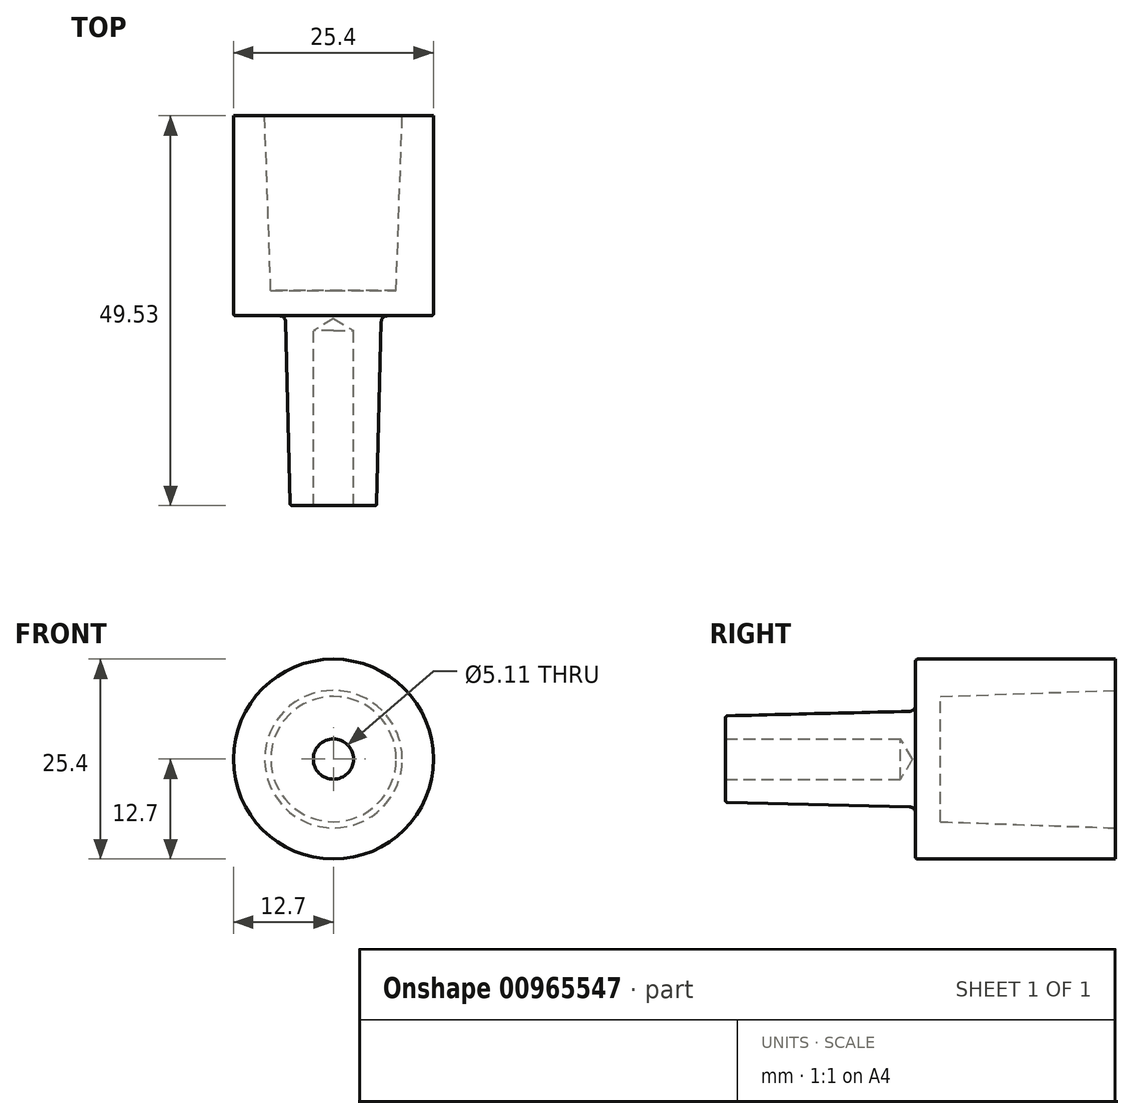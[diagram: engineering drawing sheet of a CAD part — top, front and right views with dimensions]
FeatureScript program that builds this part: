
annotation { "Feature Type Name" : "Feature", "Feature Type Description" : "" }
export const myFeature = defineFeature(function(context is Context, id is Id, definition is map)
    precondition{}
    {
        {
            var Q0;
            Q0=qCreatedBy(makeId("Right.planeOp"),FACE);
            var sketch = newSketch(context, id + "F0", { "sketchPlane" : qUnion([Q0])});
            skLineSegment(sketch, "E0", {"start": v(25.4, 0) * mm, "end": v(25.4, 12.7) * mm});
            skLineSegment(sketch, "E1", {"start": v(25.4, 12.7) * mm, "end": v(0, 12.7) * mm});
            skLineSegment(sketch, "E2", {"start": v(0, 12.7) * mm, "end": v(0, 6.1) * mm});
            skLineSegment(sketch, "E3", {"start": v(0, 6.1) * mm, "end": v(-24.13, 5.5) * mm});
            skLineSegment(sketch, "E4", {"start": v(-24.13, 5.5) * mm, "end": v(-24.13, 0) * mm});
            skLineSegment(sketch, "E5", {"start": v(-24.13, 0) * mm, "end": v(25.4, 0) * mm});
            skLineSegment(sketch, "E6", {"start": v(-59.9, 0) * mm, "end": v(67.6, 0) * mm, "construction": true});
            skSolve(sketch);
        }
        {
            var Q0;
            Q0=qSketchRegion(id+"F0",true);
            var Q1;
            Q1=sQuery(id+"F0.wireOp",EDGE,"E5");
            revolve(context, id + "F1", {"surfaceOperationType" : NewSurfaceOperationType.NEW, "entities" : qUnion([Q0]), "axis" : qUnion([Q1]), "revolveType" : RevolveType.FULL});
        }
        {
            var Q0;
            Q0=makeQuery(id+"F1.opRevolve","SWEPT_FACE",FACE,{"disambiguationData":[OSD([sQuery(id+"F0.wireOp",EDGE,"E4")])]});
            var sketch = newSketch(context, id + "F2", { "sketchPlane" : qUnion([Q0])});
            skPoint(sketch, "E7", {"position": v(0, 0) * mm});
            skSolve(sketch);
        }
        {
            var Q0;
            Q0=sQuery(id+"F2.wireOp",VERTEX,"E7");
            var Q1;
            Q1=makeQuery(id+"F1.opRevolve","SWEPT_BODY",BODY,{"disambiguationData":[OSD([sQuery(id+"F0.wireOp",EDGE,"E0"),sQuery(id+"F0.wireOp",EDGE,"E1"),sQuery(id+"F0.wireOp",EDGE,"E2"),sQuery(id+"F0.wireOp",EDGE,"E3"),sQuery(id+"F0.wireOp",EDGE,"E4"),sQuery(id+"F0.wireOp",EDGE,"E5")])]});
            hole(context, id + "F3", {"style" : HoleStyle.SIMPLE, "endStyle" : HoleEndStyle.BLIND, "standardTappedOrClearance" : lookupTablePath({ "standard" : "ANSI", "engagement" : "75%", "pitch" : "20 tpi", "size" : "1/4", "type" : "Tapped" }), "standardBlindInLast" : lookupTablePath({ "standard" : "ANSI", "engagement" : "75%", "pitch" : "20 tpi", "size" : "1/4", "type" : "Tapped" }), "holeDiameter" : 5.1 * mm, "showTappedDepth" : true, "holeDepth" : 22.22 * mm, "isTappedThrough" : true, "tappedDepth" : 18.41 * mm, "tapClearance" : 3, "startFromSketch" : true, "locations" : qUnion([Q0]), "scope" : qUnion([Q1]), "majorDiameter" : 6.35 * mm});
        }
        {
            var Q0;
            Q0=makeQuery(id+"F1.opRevolve","SWEPT_EDGE",EDGE,{"disambiguationData":[OSD([sQuery(id+"F0.wireOp",EDGE,"E2"),sQuery(id+"F0.wireOp",EDGE,"E3")])]});
            fillet(context, id + "F4", {"entities" : qUnion([Q0]), "radius" : 0.76 * mm, "tangentPropagation" : true, "allowEdgeOverflow" : false});
        }
        {
            var Q0;
            Q0=makeQuery(id+"F1.opRevolve","SWEPT_EDGE",EDGE,{"disambiguationData":[OSD([sQuery(id+"F0.wireOp",EDGE,"E1"),sQuery(id+"F0.wireOp",EDGE,"E2")])]});
            var Q1;
            Q1=makeQuery(id+"F1.opRevolve","SWEPT_EDGE",EDGE,{"disambiguationData":[OSD([sQuery(id+"F0.wireOp",EDGE,"E3"),sQuery(id+"F0.wireOp",EDGE,"E4")])]});
            fillet(context, id + "F5", {"entities" : qUnion([Q0, Q1]), "radius" : 0.25 * mm, "tangentPropagation" : true, "allowEdgeOverflow" : false});
        }
        {
            var Q0;
            Q0=qCreatedBy(makeId("Right.planeOp"),FACE);
            var sketch = newSketch(context, id + "F6", { "sketchPlane" : qUnion([Q0])});
            skLineSegment(sketch, "E8.bottom", {"start": v(25.4, 0) * mm, "end": v(3.18, 0) * mm});
            skLineSegment(sketch, "E8.top", {"start": v(25.4, 8.74) * mm, "end": v(3.18, 7.96) * mm});
            skLineSegment(sketch, "E8.left", {"start": v(25.4, 0) * mm, "end": v(25.4, 8.74) * mm});
            skLineSegment(sketch, "E8.right", {"start": v(3.18, 0) * mm, "end": v(3.18, 7.96) * mm});
            skLineSegment(sketch, "E9", {"start": v(0.13, 0) * mm, "end": v(-33.18, 0) * mm, "construction": true});
            skSolve(sketch);
        }
        {
            var Q0;
            Q0=qSketchRegion(id+"F6",true);
            var Q1;
            Q1=sQuery(id+"F6.wireOp",EDGE,"E8.bottom");
            revolve(context, id + "F7", {"operationType" : NewBodyOperationType.REMOVE, "surfaceOperationType" : NewSurfaceOperationType.NEW, "entities" : qUnion([Q0]), "axis" : qUnion([Q1]), "revolveType" : RevolveType.FULL, "oppositeDirection" : true});
        }
    });
